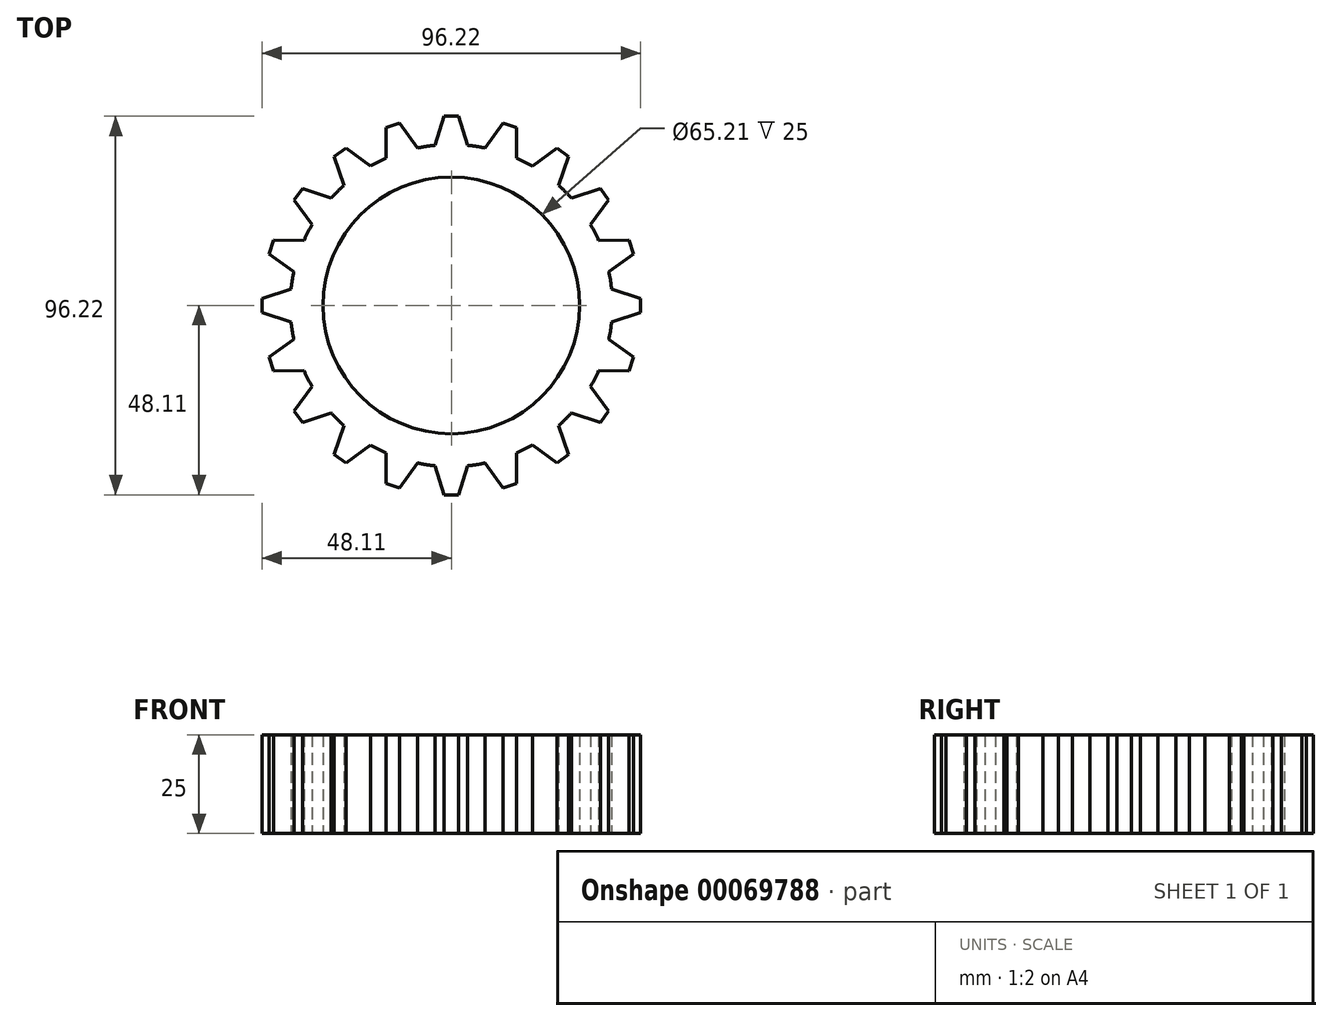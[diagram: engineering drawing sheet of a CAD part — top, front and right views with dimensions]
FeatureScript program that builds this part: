
annotation { "Feature Type Name" : "Feature", "Feature Type Description" : "" }
export const myFeature = defineFeature(function(context is Context, id is Id, definition is map)
    precondition{}
    {
        {
            var Q0;
            Q0=qCreatedBy(makeId("Top.planeOp"),FACE);
            var sketch = newSketch(context, id + "F0", { "sketchPlane" : qUnion([Q0])});
            skLineSegment(sketch, "E0", {"start": v(0, 0) * mm, "end": v(0, 50) * mm});
            skSolve(sketch);
        }
        {
            var Q0;
            Q0=qCreatedBy(makeId("Top.planeOp"),FACE);
            var sketch = newSketch(context, id + "F1", { "sketchPlane" : qUnion([Q0])});
            skLineSegment(sketch, "E1", {"start": v(0, -48.1) * mm, "end": v(1.83, -48.1) * mm});
            skArc(sketch, "E2", {"start": v(4.15, -40.72) * mm, "mid": v(6.4, -40.43) * mm, "end": v(8.63, -40.01) * mm});
            skLineSegment(sketch, "E3", {"start": v(0, 0) * mm, "end": v(0, -66.5) * mm});
            skLineSegment(sketch, "E4.MirrorCS", {"start": v(0, -48.1) * mm, "end": v(-1.83, -48.1) * mm});
            skLineSegment(sketch, "E5.1.0", {"start": v(14.87, -45.75) * mm, "end": v(13.13, -46.32) * mm});
            skLineSegment(sketch, "E5.1.1", {"start": v(14.87, -45.75) * mm, "end": v(16.6, -45.19) * mm});
            skLineSegment(sketch, "E5.2.0", {"start": v(28.28, -38.92) * mm, "end": v(26.8, -40) * mm});
            skLineSegment(sketch, "E5.2.1", {"start": v(28.28, -38.92) * mm, "end": v(29.76, -37.84) * mm});
            skLineSegment(sketch, "E5.3.0", {"start": v(38.92, -28.28) * mm, "end": v(37.84, -29.76) * mm});
            skLineSegment(sketch, "E5.3.1", {"start": v(38.92, -28.28) * mm, "end": v(40, -26.8) * mm});
            skLineSegment(sketch, "E5.4.0", {"start": v(45.75, -14.87) * mm, "end": v(45.19, -16.6) * mm});
            skLineSegment(sketch, "E5.4.1", {"start": v(45.75, -14.87) * mm, "end": v(46.32, -13.13) * mm});
            skLineSegment(sketch, "E5.5.0", {"start": v(48.1, 0) * mm, "end": v(48.1, -1.83) * mm});
            skLineSegment(sketch, "E5.5.1", {"start": v(48.1, 0) * mm, "end": v(48.1, 1.83) * mm});
            skLineSegment(sketch, "E5.6.0", {"start": v(45.75, 14.87) * mm, "end": v(46.32, 13.13) * mm});
            skLineSegment(sketch, "E5.6.1", {"start": v(45.75, 14.87) * mm, "end": v(45.19, 16.6) * mm});
            skLineSegment(sketch, "E5.7.0", {"start": v(38.92, 28.28) * mm, "end": v(40, 26.8) * mm});
            skLineSegment(sketch, "E5.7.1", {"start": v(38.92, 28.28) * mm, "end": v(37.84, 29.76) * mm});
            skLineSegment(sketch, "E5.8.0", {"start": v(28.28, 38.92) * mm, "end": v(29.76, 37.84) * mm});
            skLineSegment(sketch, "E5.8.1", {"start": v(28.28, 38.92) * mm, "end": v(26.8, 40) * mm});
            skLineSegment(sketch, "E5.9.0", {"start": v(14.87, 45.75) * mm, "end": v(16.6, 45.19) * mm});
            skLineSegment(sketch, "E5.9.1", {"start": v(14.87, 45.75) * mm, "end": v(13.13, 46.32) * mm});
            skLineSegment(sketch, "E5.10.0", {"start": v(0, 48.1) * mm, "end": v(1.83, 48.1) * mm});
            skLineSegment(sketch, "E5.10.1", {"start": v(0, 48.1) * mm, "end": v(-1.83, 48.1) * mm});
            skLineSegment(sketch, "E5.11.0", {"start": v(-14.87, 45.75) * mm, "end": v(-13.13, 46.32) * mm});
            skLineSegment(sketch, "E5.11.1", {"start": v(-14.87, 45.75) * mm, "end": v(-16.6, 45.19) * mm});
            skLineSegment(sketch, "E5.12.0", {"start": v(-28.28, 38.92) * mm, "end": v(-26.8, 40) * mm});
            skLineSegment(sketch, "E5.12.1", {"start": v(-28.28, 38.92) * mm, "end": v(-29.76, 37.84) * mm});
            skLineSegment(sketch, "E5.13.0", {"start": v(-38.92, 28.28) * mm, "end": v(-37.84, 29.76) * mm});
            skLineSegment(sketch, "E5.13.1", {"start": v(-38.92, 28.28) * mm, "end": v(-40, 26.8) * mm});
            skLineSegment(sketch, "E5.14.0", {"start": v(-45.75, 14.87) * mm, "end": v(-45.19, 16.6) * mm});
            skLineSegment(sketch, "E5.14.1", {"start": v(-45.75, 14.87) * mm, "end": v(-46.32, 13.13) * mm});
            skLineSegment(sketch, "E5.15.0", {"start": v(-48.1, 0) * mm, "end": v(-48.1, 1.83) * mm});
            skLineSegment(sketch, "E5.15.1", {"start": v(-48.1, 0) * mm, "end": v(-48.1, -1.83) * mm});
            skLineSegment(sketch, "E5.16.0", {"start": v(-45.75, -14.87) * mm, "end": v(-46.32, -13.13) * mm});
            skLineSegment(sketch, "E5.16.1", {"start": v(-45.75, -14.87) * mm, "end": v(-45.19, -16.6) * mm});
            skLineSegment(sketch, "E5.17.0", {"start": v(-38.92, -28.28) * mm, "end": v(-40, -26.8) * mm});
            skLineSegment(sketch, "E5.17.1", {"start": v(-38.92, -28.28) * mm, "end": v(-37.84, -29.76) * mm});
            skLineSegment(sketch, "E5.18.0", {"start": v(-28.28, -38.92) * mm, "end": v(-29.76, -37.84) * mm});
            skLineSegment(sketch, "E5.18.1", {"start": v(-28.28, -38.92) * mm, "end": v(-26.8, -40) * mm});
            skLineSegment(sketch, "E5.19.0", {"start": v(-14.87, -45.75) * mm, "end": v(-16.6, -45.19) * mm});
            skLineSegment(sketch, "E5.19.1", {"start": v(-14.87, -45.75) * mm, "end": v(-13.13, -46.32) * mm});
            skPoint(sketch, "E6.orphan", {"position": v(-3.48, -40.78) * mm});
            skPoint(sketch, "E7.orphan", {"position": v(3.48, -40.78) * mm});
            skLineSegment(sketch, "E8", {"start": v(-4.15, -40.72) * mm, "end": v(-1.83, -48.1) * mm});
            skLineSegment(sketch, "E9", {"start": v(1.83, -48.1) * mm, "end": v(4.15, -40.72) * mm});
            skLineSegment(sketch, "E10.1.0", {"start": v(8.63, -40.01) * mm, "end": v(13.13, -46.32) * mm});
            skLineSegment(sketch, "E10.1.1", {"start": v(16.6, -45.19) * mm, "end": v(16.53, -37.44) * mm});
            skLineSegment(sketch, "E10.2.0", {"start": v(20.57, -35.38) * mm, "end": v(26.8, -40) * mm});
            skLineSegment(sketch, "E10.2.1", {"start": v(29.76, -37.84) * mm, "end": v(27.3, -30.5) * mm});
            skLineSegment(sketch, "E10.3.0", {"start": v(30.5, -27.3) * mm, "end": v(37.84, -29.76) * mm});
            skLineSegment(sketch, "E10.3.1", {"start": v(40, -26.8) * mm, "end": v(35.38, -20.57) * mm});
            skLineSegment(sketch, "E10.4.0", {"start": v(37.44, -16.53) * mm, "end": v(45.19, -16.6) * mm});
            skLineSegment(sketch, "E10.4.1", {"start": v(46.32, -13.13) * mm, "end": v(40.01, -8.63) * mm});
            skLineSegment(sketch, "E10.5.0", {"start": v(40.72, -4.15) * mm, "end": v(48.1, -1.83) * mm});
            skLineSegment(sketch, "E10.5.1", {"start": v(48.1, 1.83) * mm, "end": v(40.72, 4.15) * mm});
            skLineSegment(sketch, "E10.6.0", {"start": v(40.01, 8.63) * mm, "end": v(46.32, 13.13) * mm});
            skLineSegment(sketch, "E10.6.1", {"start": v(45.19, 16.6) * mm, "end": v(37.44, 16.53) * mm});
            skLineSegment(sketch, "E10.7.0", {"start": v(35.38, 20.57) * mm, "end": v(40, 26.8) * mm});
            skLineSegment(sketch, "E10.7.1", {"start": v(37.84, 29.76) * mm, "end": v(30.5, 27.3) * mm});
            skLineSegment(sketch, "E10.8.0", {"start": v(27.3, 30.5) * mm, "end": v(29.76, 37.84) * mm});
            skLineSegment(sketch, "E10.8.1", {"start": v(26.8, 40) * mm, "end": v(20.57, 35.38) * mm});
            skLineSegment(sketch, "E10.9.0", {"start": v(16.53, 37.44) * mm, "end": v(16.6, 45.19) * mm});
            skLineSegment(sketch, "E10.9.1", {"start": v(13.13, 46.32) * mm, "end": v(8.63, 40.01) * mm});
            skLineSegment(sketch, "E10.10.0", {"start": v(4.15, 40.72) * mm, "end": v(1.83, 48.1) * mm});
            skLineSegment(sketch, "E10.10.1", {"start": v(-1.83, 48.1) * mm, "end": v(-4.15, 40.72) * mm});
            skLineSegment(sketch, "E10.11.0", {"start": v(-8.63, 40.01) * mm, "end": v(-13.13, 46.32) * mm});
            skLineSegment(sketch, "E10.11.1", {"start": v(-16.6, 45.19) * mm, "end": v(-16.53, 37.44) * mm});
            skLineSegment(sketch, "E10.12.0", {"start": v(-20.57, 35.38) * mm, "end": v(-26.8, 40) * mm});
            skLineSegment(sketch, "E10.12.1", {"start": v(-29.76, 37.84) * mm, "end": v(-27.3, 30.5) * mm});
            skLineSegment(sketch, "E10.13.0", {"start": v(-30.5, 27.3) * mm, "end": v(-37.84, 29.76) * mm});
            skLineSegment(sketch, "E10.13.1", {"start": v(-40, 26.8) * mm, "end": v(-35.38, 20.57) * mm});
            skLineSegment(sketch, "E10.14.0", {"start": v(-37.44, 16.53) * mm, "end": v(-45.19, 16.6) * mm});
            skLineSegment(sketch, "E10.14.1", {"start": v(-46.32, 13.13) * mm, "end": v(-40.01, 8.63) * mm});
            skLineSegment(sketch, "E10.15.0", {"start": v(-40.72, 4.15) * mm, "end": v(-48.1, 1.83) * mm});
            skLineSegment(sketch, "E10.15.1", {"start": v(-48.1, -1.83) * mm, "end": v(-40.72, -4.15) * mm});
            skLineSegment(sketch, "E10.16.0", {"start": v(-40.01, -8.63) * mm, "end": v(-46.32, -13.13) * mm});
            skLineSegment(sketch, "E10.16.1", {"start": v(-45.19, -16.6) * mm, "end": v(-37.44, -16.53) * mm});
            skLineSegment(sketch, "E10.17.0", {"start": v(-35.38, -20.57) * mm, "end": v(-40, -26.8) * mm});
            skLineSegment(sketch, "E10.17.1", {"start": v(-37.84, -29.76) * mm, "end": v(-30.5, -27.3) * mm});
            skLineSegment(sketch, "E10.18.0", {"start": v(-27.3, -30.5) * mm, "end": v(-29.76, -37.84) * mm});
            skLineSegment(sketch, "E10.18.1", {"start": v(-26.8, -40) * mm, "end": v(-20.57, -35.38) * mm});
            skLineSegment(sketch, "E10.19.0", {"start": v(-16.53, -37.44) * mm, "end": v(-16.6, -45.19) * mm});
            skLineSegment(sketch, "E10.19.1", {"start": v(-13.13, -46.32) * mm, "end": v(-8.63, -40.01) * mm});
            skArc(sketch, "E11.trimOffspring", {"start": v(-8.63, -40.01) * mm, "mid": v(-6.4, -40.43) * mm, "end": v(-4.15, -40.72) * mm});
            skArc(sketch, "E12.trimOffspring", {"start": v(16.53, -37.44) * mm, "mid": v(18.58, -36.47) * mm, "end": v(20.57, -35.38) * mm});
            skArc(sketch, "E13.trimOffspring", {"start": v(27.3, -30.5) * mm, "mid": v(28.94, -28.94) * mm, "end": v(30.5, -27.3) * mm});
            skArc(sketch, "E14.trimOffspring", {"start": v(35.38, -20.57) * mm, "mid": v(36.47, -18.58) * mm, "end": v(37.44, -16.53) * mm});
            skArc(sketch, "E15.trimOffspring", {"start": v(40.01, -8.63) * mm, "mid": v(40.43, -6.4) * mm, "end": v(40.72, -4.15) * mm});
            skArc(sketch, "E16.trimOffspring", {"start": v(40.72, 4.15) * mm, "mid": v(40.43, 6.4) * mm, "end": v(40.01, 8.63) * mm});
            skArc(sketch, "E17.trimOffspring", {"start": v(37.44, 16.53) * mm, "mid": v(36.47, 18.58) * mm, "end": v(35.38, 20.57) * mm});
            skArc(sketch, "E18.trimOffspring", {"start": v(30.5, 27.3) * mm, "mid": v(28.94, 28.94) * mm, "end": v(27.3, 30.5) * mm});
            skArc(sketch, "E19.trimOffspring", {"start": v(20.57, 35.38) * mm, "mid": v(18.58, 36.47) * mm, "end": v(16.53, 37.44) * mm});
            skArc(sketch, "E20.trimOffspring", {"start": v(8.63, 40.01) * mm, "mid": v(6.4, 40.43) * mm, "end": v(4.15, 40.72) * mm});
            skArc(sketch, "E21.trimOffspring", {"start": v(-4.15, 40.72) * mm, "mid": v(-6.4, 40.43) * mm, "end": v(-8.63, 40.01) * mm});
            skArc(sketch, "E22.trimOffspring", {"start": v(-16.53, 37.44) * mm, "mid": v(-18.58, 36.47) * mm, "end": v(-20.57, 35.38) * mm});
            skArc(sketch, "E23.trimOffspring", {"start": v(-27.3, 30.5) * mm, "mid": v(-28.94, 28.94) * mm, "end": v(-30.5, 27.3) * mm});
            skArc(sketch, "E24.trimOffspring", {"start": v(-35.38, 20.57) * mm, "mid": v(-36.47, 18.58) * mm, "end": v(-37.44, 16.53) * mm});
            skArc(sketch, "E25.trimOffspring", {"start": v(-40.01, 8.63) * mm, "mid": v(-40.43, 6.4) * mm, "end": v(-40.72, 4.15) * mm});
            skArc(sketch, "E26.trimOffspring", {"start": v(-40.72, -4.15) * mm, "mid": v(-40.43, -6.4) * mm, "end": v(-40.01, -8.63) * mm});
            skArc(sketch, "E27.trimOffspring", {"start": v(-37.44, -16.53) * mm, "mid": v(-36.47, -18.58) * mm, "end": v(-35.38, -20.57) * mm});
            skArc(sketch, "E28.trimOffspring", {"start": v(-30.5, -27.3) * mm, "mid": v(-28.94, -28.94) * mm, "end": v(-27.3, -30.5) * mm});
            skArc(sketch, "E29.trimOffspring", {"start": v(-20.57, -35.38) * mm, "mid": v(-18.58, -36.47) * mm, "end": v(-16.53, -37.44) * mm});
            skCircle(sketch, "E30", {"center": v(0, 0) * mm, "radius": 32.6 * mm});
            skSolve(sketch);
        }
        {
            var Q0;
            Q0=makeQuery(id+"F1.imprint","IMPRINT",FACE,{"disambiguationData":[TD([[makeQuery(id+"F1.imprint","IMPRINT",EDGE,{"derivedFrom":sQuery(id+"F1.wireOp",EDGE,"E1")}),1.0]])]});
            extrude(context, id + "F2", {"entities" : qUnion([Q0]), "depth" : 25 * mm});
        }
    });
